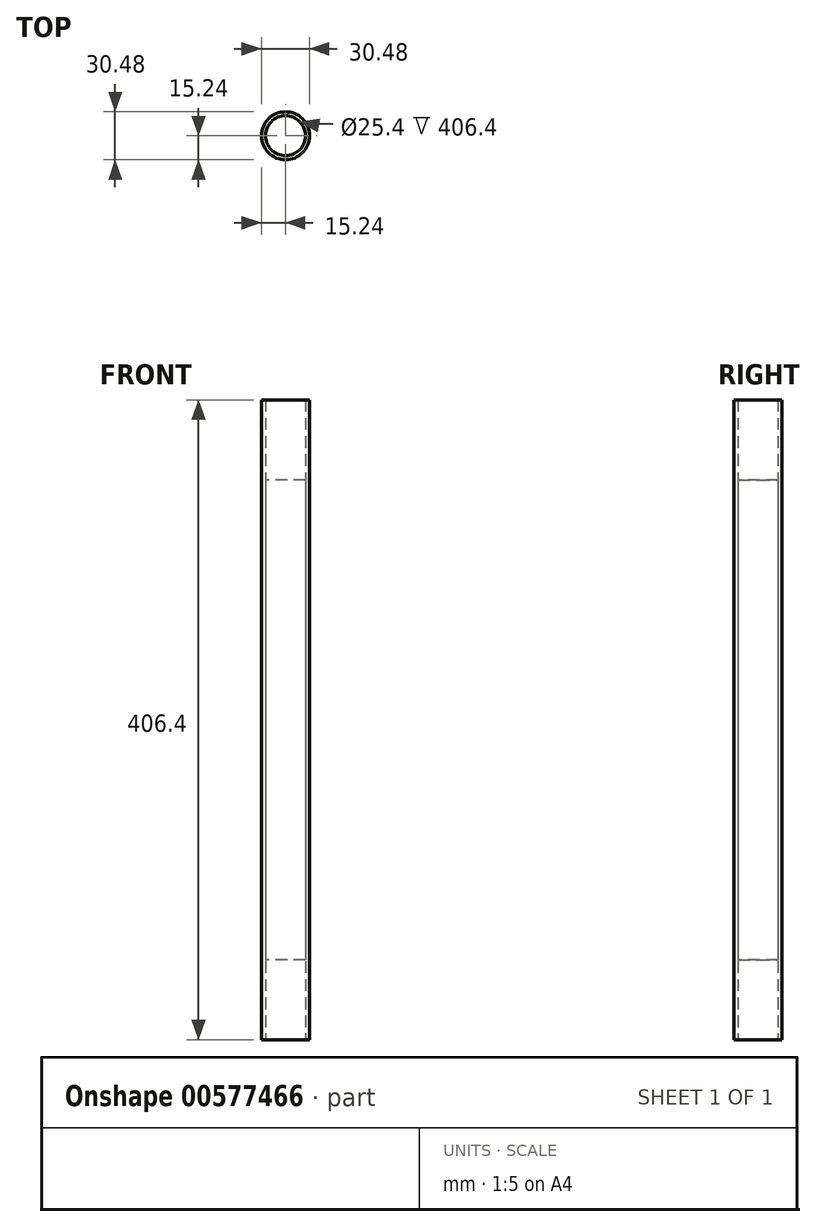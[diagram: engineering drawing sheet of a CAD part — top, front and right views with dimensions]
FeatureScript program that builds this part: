
annotation { "Feature Type Name" : "Feature", "Feature Type Description" : "" }
export const myFeature = defineFeature(function(context is Context, id is Id, definition is map)
    precondition{}
    {
        {
            var Q0;
            Q0=qCreatedBy(makeId("Top.planeOp"),FACE);
            var sketch = newSketch(context, id + "F0", { "sketchPlane" : qUnion([Q0])});
            skCircle(sketch, "E0", {"center": v(0, 0) * mm, "radius": 12.7 * mm});
            skSolve(sketch);
        }
        {
            var Q0;
            Q0 = qSketchRegion(id + "F0", true);
            extrude(context, id + "F1", {"entities" : qUnion([Q0]), "endBound" : BoundingType.SYMMETRIC, "depth" : 304.8 * mm, "offsetDistance" : 25.4 * mm});
        }
        {
            var Q0;
            Q0=qCreatedBy(makeId("Top.planeOp"),FACE);
            var sketch = newSketch(context, id + "F2", { "sketchPlane" : qUnion([Q0])});
            skCircle(sketch, "E1.0", {"center": v(0, 0) * mm, "radius": 12.7 * mm, "construction": true});
            skCircle(sketch, "E2", {"center": v(0, 0) * mm, "radius": 12.7 * mm});
            skCircle(sketch, "E3", {"center": v(0, 0) * mm, "radius": 15.24 * mm});
            skSolve(sketch);
        }
        {
            var Q0;
            Q0 = qSketchRegion(id + "F2", true);
            extrude(context, id + "F3", {"entities" : qUnion([Q0]), "endBound" : BoundingType.SYMMETRIC, "depth" : 406.4 * mm, "offsetDistance" : 25.4 * mm});
        }
    });
